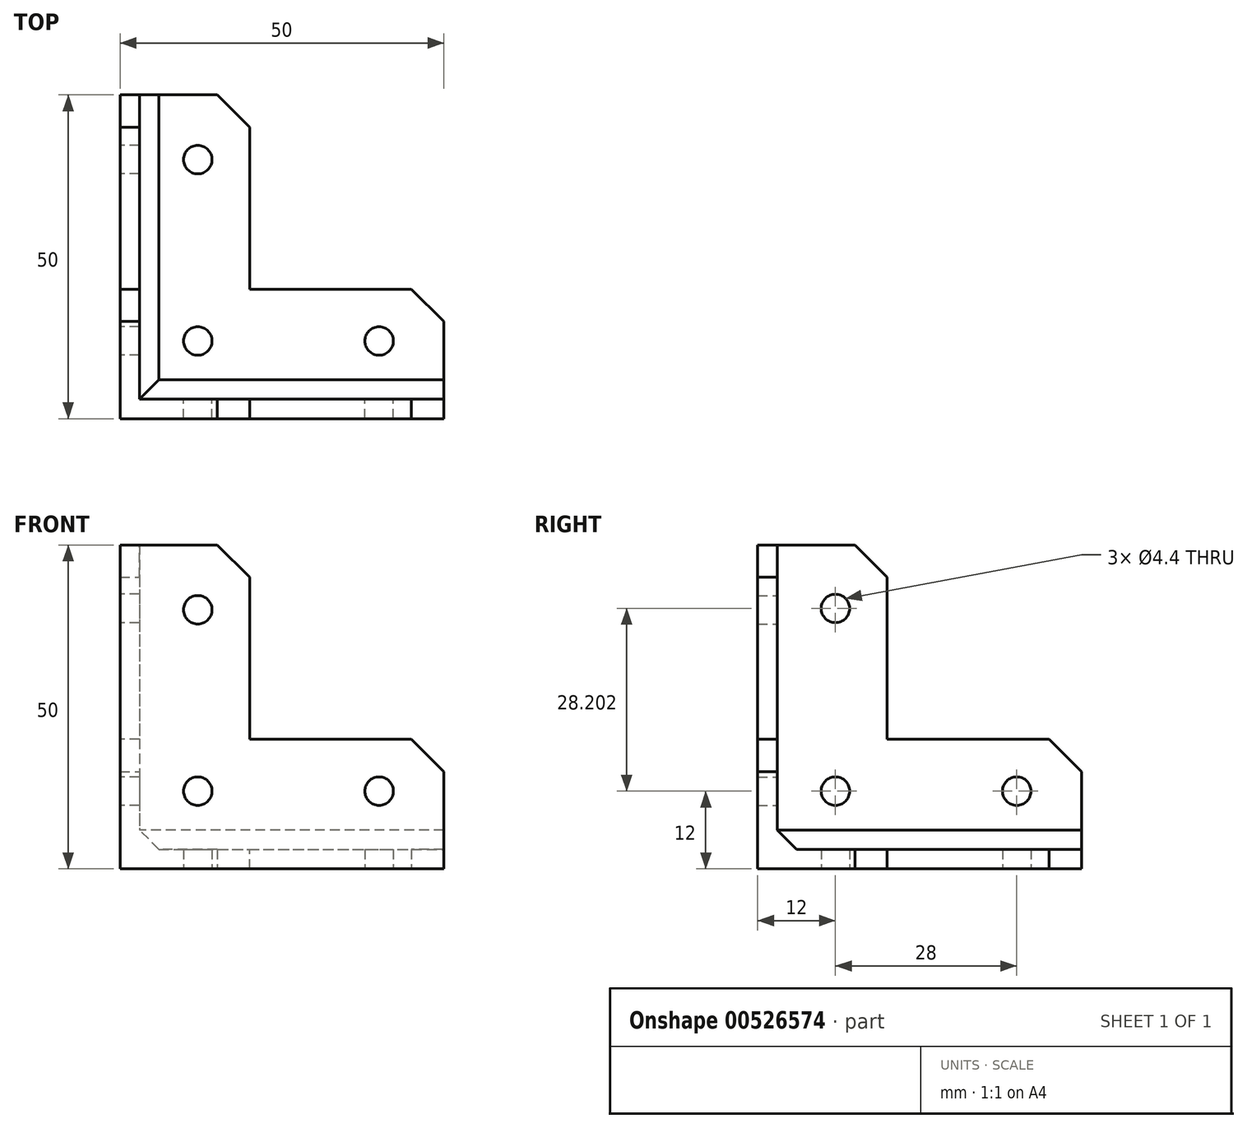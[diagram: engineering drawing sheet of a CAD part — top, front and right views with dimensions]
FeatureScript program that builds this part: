
annotation { "Feature Type Name" : "Feature", "Feature Type Description" : "" }
export const myFeature = defineFeature(function(context is Context, id is Id, definition is map)
    precondition{}
    {
        {
            var Q0;
            Q0=qCreatedBy(makeId("Front.planeOp"),FACE);
            var sketch = newSketch(context, id + "F0", { "sketchPlane" : qUnion([Q0])});
            skLineSegment(sketch, "E0", {"start": v(-103.1, 50) * mm, "end": v(-103.1, 0) * mm});
            skLineSegment(sketch, "E1", {"start": v(-103.1, 0) * mm, "end": v(-53.1, 0) * mm});
            skLineSegment(sketch, "E2", {"start": v(-53.1, 0) * mm, "end": v(-53.1, 20) * mm});
            skLineSegment(sketch, "E3", {"start": v(-53.1, 20) * mm, "end": v(-83.1, 20) * mm});
            skLineSegment(sketch, "E4", {"start": v(-83.1, 20) * mm, "end": v(-83.1, 50) * mm});
            skLineSegment(sketch, "E5", {"start": v(-83.1, 50) * mm, "end": v(-103.1, 50) * mm});
            skPoint(sketch, "E6", {"position": v(-91.1, 40) * mm});
            skPoint(sketch, "E6.positionSnap0", {"position": v(-93.1, 50) * mm});
            skPoint(sketch, "E7", {"position": v(-91.1, 12) * mm});
            skPoint(sketch, "E8", {"position": v(-63.1, 12) * mm});
            skPoint(sketch, "E8.positionSnap0", {"position": v(-53.1, 10) * mm});
            skSolve(sketch);
        }
        {
            var Q0;
            Q0 = qSketchRegion(id + "F0", true);
            extrude(context, id + "F1", {"entities" : qUnion([Q0]), "depth" : 3 * mm, "offsetDistance" : 25 * mm});
        }
        {
            var Q0;
            Q0=makeQuery(id+"F1.opExtrude","SWEPT_FACE",FACE,{"disambiguationData":[OSD([sQuery(id+"F0.wireOp",EDGE,"E0")])]});
            var sketch = newSketch(context, id + "F2", { "sketchPlane" : qUnion([Q0])});
            skLineSegment(sketch, "E9", {"start": v(3, 50) * mm, "end": v(-17, 50) * mm});
            skLineSegment(sketch, "E10", {"start": v(-17, 50) * mm, "end": v(-17, 20) * mm});
            skLineSegment(sketch, "E11", {"start": v(-17, 20) * mm, "end": v(-47, 20) * mm});
            skLineSegment(sketch, "E12", {"start": v(-47, 20) * mm, "end": v(-47, 0) * mm});
            skLineSegment(sketch, "E13", {"start": v(-47, 0) * mm, "end": v(3, 0) * mm});
            skPoint(sketch, "E14", {"position": v(-9, 40.2) * mm});
            skPoint(sketch, "E14.positionSnap0", {"position": v(-7, 50) * mm});
            skPoint(sketch, "E15", {"position": v(-37, 12) * mm});
            skPoint(sketch, "E15.positionSnap0", {"position": v(-47, 10) * mm});
            skPoint(sketch, "E16", {"position": v(-9, 12) * mm});
            skSolve(sketch);
        }
        {
            var Q0;
            {var subQ1=sQuery(id+"F2.wireOp",EDGE,"E10");Q0=makeQuery(id+"F2.imprint","IMPRINT",FACE,{"disambiguationData":[TD([[makeQuery(id+"F2.imprint","IMPRINT",EDGE,{"derivedFrom":subQ1}),1.0]])]});}
            extrude(context, id + "F3", {"entities" : qUnion([Q0]), "operationType" : NewBodyOperationType.ADD, "oppositeDirection" : true, "depth" : 3 * mm, "offsetDistance" : 25 * mm});
        }
        {
            var Q0;
            Q0=makeQuery(id+"F3.boolean.opBoolean","MERGE",FACE,{"derivedFrom":[makeQuery(id+"F1.opExtrude","SWEPT_FACE",FACE,{"disambiguationData":[OSD([sQuery(id+"F0.wireOp",EDGE,"E1")])]}),makeQuery(id+"F3.opExtrude","SWEPT_FACE",FACE,{"disambiguationData":[OSD([sQuery(id+"F2.wireOp",EDGE,"E13")])]})]});
            var sketch = newSketch(context, id + "F4", { "sketchPlane" : qUnion([Q0])});
            skLineSegment(sketch, "E17", {"start": v(-53.1, 3) * mm, "end": v(-103.1, 3) * mm});
            skLineSegment(sketch, "E18", {"start": v(-103.1, 3) * mm, "end": v(-103.1, -47) * mm});
            skLineSegment(sketch, "E19", {"start": v(-103.1, -47) * mm, "end": v(-83.1, -47) * mm});
            skLineSegment(sketch, "E20", {"start": v(-83.1, -47) * mm, "end": v(-83.1, -17) * mm});
            skLineSegment(sketch, "E21", {"start": v(-83.1, -17) * mm, "end": v(-53.1, -17) * mm});
            skLineSegment(sketch, "E22", {"start": v(-53.1, -17) * mm, "end": v(-53.1, 3) * mm});
            skPoint(sketch, "E23", {"position": v(-63.1, -9) * mm});
            skPoint(sketch, "E23.positionSnap0", {"position": v(-53.1, -7) * mm});
            skPoint(sketch, "E24", {"position": v(-91.1, -37) * mm});
            skPoint(sketch, "E24.positionSnap0", {"position": v(-93.1, -47) * mm});
            skPoint(sketch, "E25", {"position": v(-91.1, -9) * mm});
            skSolve(sketch);
        }
        {
            var Q0;
            Q0 = qSketchRegion(id + "F4", true);
            extrude(context, id + "F5", {"entities" : qUnion([Q0]), "operationType" : NewBodyOperationType.ADD, "oppositeDirection" : true, "depth" : 3 * mm, "offsetDistance" : 25 * mm});
        }
        {
            var Q0;
            Q0=sQuery(id+"F0.wireOp",VERTEX,"E8");
            var Q1;
            Q1=sQuery(id+"F0.wireOp",VERTEX,"E6");
            var Q2;
            Q2=sQuery(id+"F0.wireOp",VERTEX,"E7");
            var Q3;
            Q3=makeQuery(id+"F1.opExtrude","SWEPT_BODY",BODY,{"disambiguationData":[OSD([sQuery(id+"F0.wireOp",EDGE,"E0"),sQuery(id+"F0.wireOp",EDGE,"E1"),sQuery(id+"F0.wireOp",EDGE,"E2"),sQuery(id+"F0.wireOp",EDGE,"E3"),sQuery(id+"F0.wireOp",EDGE,"E4"),sQuery(id+"F0.wireOp",EDGE,"E5")])]});
            hole(context, id + "F6", {"style" : HoleStyle.SIMPLE, "endStyle" : HoleEndStyle.BLIND, "oppositeDirection" : true, "standardTappedOrClearance" : lookupTablePath({ "standard" : "ISO", "fit" : "Normal", "size" : "M4", "type" : "Clearance" }), "standardBlindInLast" : lookupTablePath({ "fit" : "Standard", "standard" : "ISO", "size" : "M4", "type" : "Clearance" }), "holeDiameter" : 4.4 * mm, "holeDepth" : 80 * mm, "isTappedThrough" : true, "tappedDepth" : 12 * mm, "tapClearance" : 3, "startFromSketch" : true, "locations" : qUnion([Q0, Q1, Q2]), "scope" : qUnion([Q3])});
        }
        {
            var Q0;
            Q0=sQuery(id+"F2.wireOp",VERTEX,"E14");
            var Q1;
            Q1=sQuery(id+"F4.wireOp",VERTEX,"E25");
            var Q2;
            Q2=sQuery(id+"F2.wireOp",VERTEX,"E15");
            var Q3;
            Q3=sQuery(id+"F2.wireOp",VERTEX,"E16");
            var Q4;
            Q4=sQuery(id+"F4.wireOp",VERTEX,"E24");
            var Q5;
            Q5=sQuery(id+"F4.wireOp",VERTEX,"E23");
            var Q6;
            Q6=makeQuery(id+"F1.opExtrude","SWEPT_BODY",BODY,{"disambiguationData":[OSD([sQuery(id+"F0.wireOp",EDGE,"E0"),sQuery(id+"F0.wireOp",EDGE,"E1"),sQuery(id+"F0.wireOp",EDGE,"E2"),sQuery(id+"F0.wireOp",EDGE,"E3"),sQuery(id+"F0.wireOp",EDGE,"E4"),sQuery(id+"F0.wireOp",EDGE,"E5")])]});
            hole(context, id + "F7", {"style" : HoleStyle.SIMPLE, "endStyle" : HoleEndStyle.BLIND, "standardTappedOrClearance" : lookupTablePath({ "standard" : "ISO", "fit" : "Normal", "size" : "M4", "type" : "Clearance" }), "standardBlindInLast" : lookupTablePath({ "fit" : "Standard", "standard" : "ISO", "size" : "M4", "type" : "Clearance" }), "holeDiameter" : 4.4 * mm, "holeDepth" : 80 * mm, "isTappedThrough" : true, "tappedDepth" : 12 * mm, "tapClearance" : 3, "startFromSketch" : true, "locations" : qUnion([Q0, Q1, Q2, Q3, Q4, Q5]), "scope" : qUnion([Q6])});
        }
        {
            var Q0;
            Q0=makeQuery(id+"F3.opExtrude","CAP_FACE",FACE,{"disambiguationData":[OSD([sQuery(id+"F0.wireOp",EDGE,"E0"),sQuery(id+"F2.wireOp",EDGE,"E9"),sQuery(id+"F2.wireOp",EDGE,"E10"),sQuery(id+"F2.wireOp",EDGE,"E11"),sQuery(id+"F2.wireOp",EDGE,"E12"),sQuery(id+"F2.wireOp",EDGE,"E13")])],"isStart":false});
            var sketch = newSketch(context, id + "F8", { "sketchPlane" : qUnion([Q0])});
            skLineSegment(sketch, "E26.bottom", {"start": v(0, 3) * mm, "end": v(5, 3) * mm});
            skLineSegment(sketch, "E26.top", {"start": v(0, 8) * mm, "end": v(5, 8) * mm});
            skLineSegment(sketch, "E26.left", {"start": v(0, 3) * mm, "end": v(0, 8) * mm});
            skLineSegment(sketch, "E26.right", {"start": v(5, 3) * mm, "end": v(5, 8) * mm});
            skSolve(sketch);
        }
        {
            var Q0;
            Q0=makeQuery(id+"F5.boolean.opBoolean","INTERSECT",EDGE,{"derivedFrom":[makeQuery(id+"F1.opExtrude","CAP_FACE",FACE,{"disambiguationData":[OSD([sQuery(id+"F0.wireOp",EDGE,"E0"),sQuery(id+"F0.wireOp",EDGE,"E1"),sQuery(id+"F0.wireOp",EDGE,"E2"),sQuery(id+"F0.wireOp",EDGE,"E3"),sQuery(id+"F0.wireOp",EDGE,"E4"),sQuery(id+"F0.wireOp",EDGE,"E5")])],"isStart":true}),makeQuery(id+"F5.opExtrude","CAP_FACE",FACE,{"disambiguationData":[OSD([sQuery(id+"F4.wireOp",EDGE,"E17"),sQuery(id+"F4.wireOp",EDGE,"E18"),sQuery(id+"F4.wireOp",EDGE,"E19"),sQuery(id+"F4.wireOp",EDGE,"E20"),sQuery(id+"F4.wireOp",EDGE,"E21"),sQuery(id+"F4.wireOp",EDGE,"E22")])],"isStart":false})]});
            var Q1;
            Q1=makeQuery(id+"F5.boolean.opBoolean","INTERSECT",EDGE,{"derivedFrom":[makeQuery(id+"F3.opExtrude","CAP_FACE",FACE,{"disambiguationData":[OSD([sQuery(id+"F0.wireOp",EDGE,"E0"),sQuery(id+"F2.wireOp",EDGE,"E9"),sQuery(id+"F2.wireOp",EDGE,"E10"),sQuery(id+"F2.wireOp",EDGE,"E11"),sQuery(id+"F2.wireOp",EDGE,"E12"),sQuery(id+"F2.wireOp",EDGE,"E13")])],"isStart":false}),makeQuery(id+"F5.opExtrude","CAP_FACE",FACE,{"disambiguationData":[OSD([sQuery(id+"F4.wireOp",EDGE,"E17"),sQuery(id+"F4.wireOp",EDGE,"E18"),sQuery(id+"F4.wireOp",EDGE,"E19"),sQuery(id+"F4.wireOp",EDGE,"E20"),sQuery(id+"F4.wireOp",EDGE,"E21"),sQuery(id+"F4.wireOp",EDGE,"E22")])],"isStart":false})]});
            var Q2;
            Q2=makeQuery(id+"F3.opExtrude","CAP_EDGE",EDGE,{"disambiguationData":[OSD([sQuery(id+"F0.wireOp",EDGE,"E0")])],"isStart":false});
            chamfer(context, id + "F9", {"entities" : qUnion([Q0, Q1, Q2]), "width" : 3 * mm, "tangentPropagation" : true});
        }
        {
            var Q0;
            Q0=makeQuery(id+"F1.opExtrude","SWEPT_EDGE",EDGE,{"disambiguationData":[OSD([sQuery(id+"F0.wireOp",EDGE,"E2"),sQuery(id+"F0.wireOp",EDGE,"E3")])]});
            var Q1;
            Q1=makeQuery(id+"F5.opExtrude","SWEPT_EDGE",EDGE,{"disambiguationData":[OSD([sQuery(id+"F4.wireOp",EDGE,"E21"),sQuery(id+"F4.wireOp",EDGE,"E22")])]});
            var Q2;
            Q2=makeQuery(id+"F5.opExtrude","SWEPT_EDGE",EDGE,{"disambiguationData":[OSD([sQuery(id+"F4.wireOp",EDGE,"E19"),sQuery(id+"F4.wireOp",EDGE,"E20")])]});
            var Q3;
            Q3=makeQuery(id+"F3.opExtrude","SWEPT_EDGE",EDGE,{"disambiguationData":[OSD([sQuery(id+"F2.wireOp",EDGE,"E11"),sQuery(id+"F2.wireOp",EDGE,"E12")])]});
            var Q4;
            Q4=makeQuery(id+"F1.opExtrude","SWEPT_EDGE",EDGE,{"disambiguationData":[OSD([sQuery(id+"F0.wireOp",EDGE,"E4"),sQuery(id+"F0.wireOp",EDGE,"E5")])]});
            var Q5;
            Q5=makeQuery(id+"F3.opExtrude","SWEPT_EDGE",EDGE,{"disambiguationData":[OSD([sQuery(id+"F2.wireOp",EDGE,"E9"),sQuery(id+"F2.wireOp",EDGE,"E10")])]});
            chamfer(context, id + "F10", {"entities" : qUnion([Q0, Q1, Q2, Q3, Q4, Q5]), "width" : 5 * mm, "tangentPropagation" : true});
        }
    });
